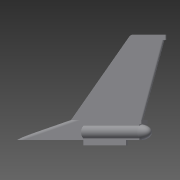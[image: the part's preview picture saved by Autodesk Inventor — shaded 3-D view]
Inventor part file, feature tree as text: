
AUTODESK INVENTOR PART (.ipt)
format: ipt  version: 2014 SP1 (Build 180222100, 222)  size: 187,392 bytes
history: native  units: mm
features: sketch x4, extrude x4, fillet x2, chamfer x1, plane x1, revolve x1
ambient origin geometry x8: Origin, YZ Plane, XZ Plane, XY Plane, X Axis, Y Axis, Z Axis, Center Point
bodies: Solid1 (feature_tree)
feature tree (13):
  sketch  "Sketch1"  dims[d0=330.0mm d1=28.0mm]
  extrude  "Extrusion1"  Depth=28.0mm
  extrude  "Extrusion2"  Depth=8.0mm
  fillet  "Fillet1"  Radius=188.0mm
  extrude  "Extrusion3"  Depth=5.0mm
  fillet  "Fillet2"  Radius=90.0mm
  extrude  "Extrusion4"  Depth=10.0mm
  chamfer  "Chamfer2"  Distance=110.0mm
  plane  "Work Plane1"
  revolve  "Revolution1"  [1 undecoded]
  sketch  "Sketch2"  dims[d2=5.0mm d3=8.0mm d4=188.0mm]
  sketch  "Sketch3"  dims[d7=10.0mm d8=5.0mm d9=90.0mm]
  sketch  "Sketch4"  dims[d10=180.0mm d11=10.0mm d12=110.0mm d13=16.0mm d14=0.0mm d15=5.0mm d16=0.0mm d17=2.5mm d18=50.0mm d19=0.0mm d23=145.0mm d24=7.9mm d25=20.0mm d26=150.0mm d27=0.0mm d28=0.0mm d29=5.9mm d30=2.0mm d31=45.0deg d32=0.0mm d33=90.0deg]
note: 1 required parameter value undecoded (feature->parameter linkage not recoverable at this tier; creation-order binding heuristic only, values carry confidence <= 0.55)
